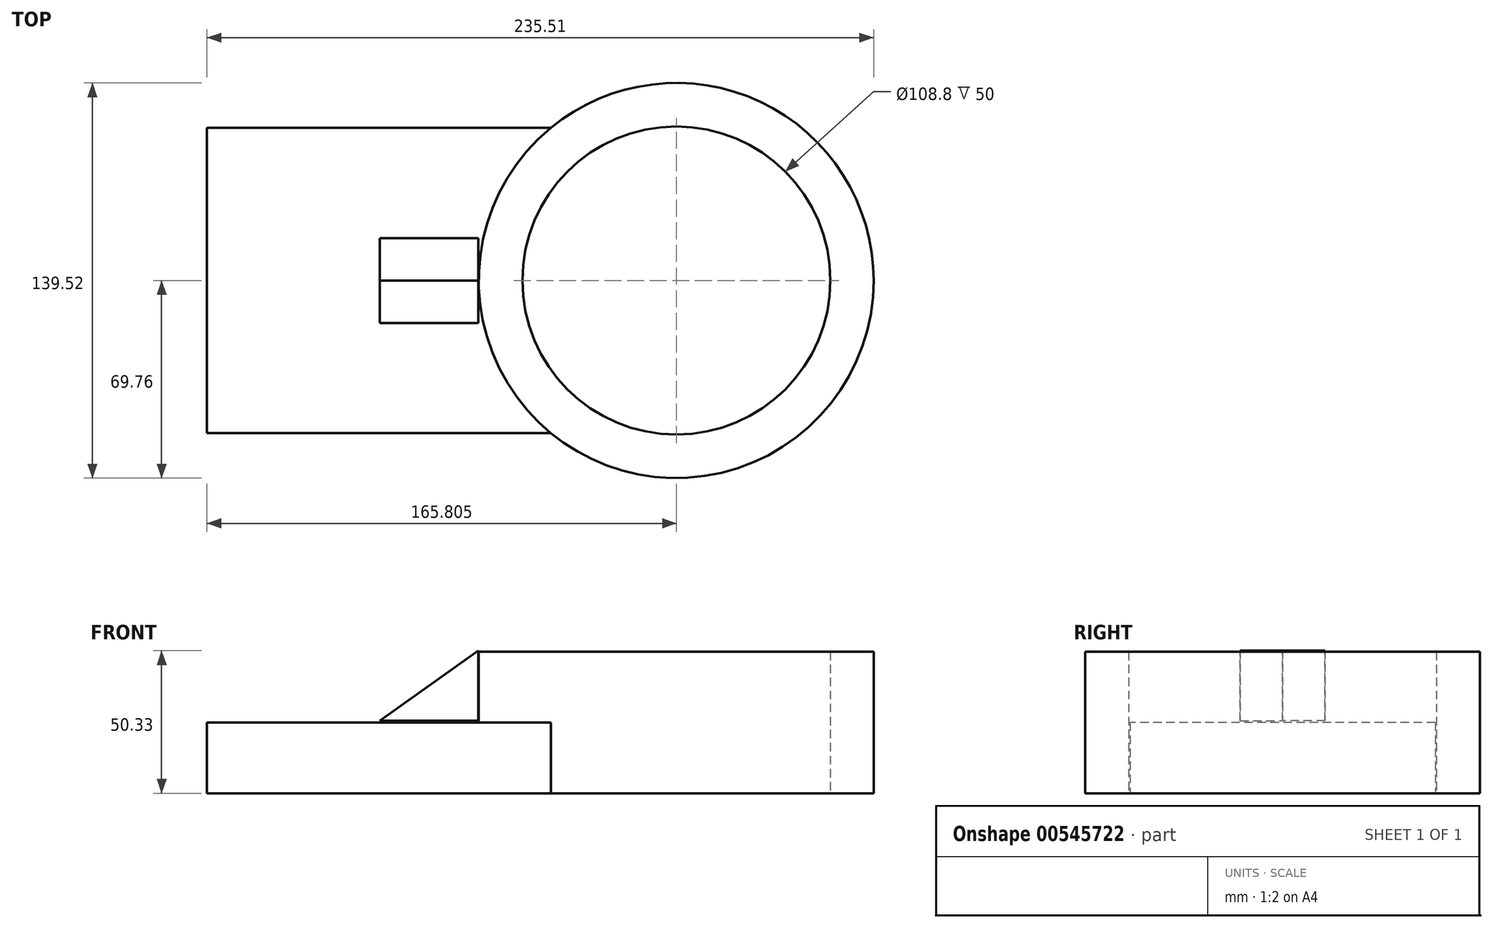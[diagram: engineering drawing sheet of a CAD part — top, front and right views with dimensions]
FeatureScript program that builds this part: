
annotation { "Feature Type Name" : "Feature", "Feature Type Description" : "" }
export const myFeature = defineFeature(function(context is Context, id is Id, definition is map)
    precondition{}
    {
        {
            var Q0;
            Q0=qCreatedBy(makeId("Top.planeOp"),FACE);
            var sketch = newSketch(context, id + "F0", { "sketchPlane" : qUnion([Q0])});
            skLineSegment(sketch, "E0.bottom", {"start": v(-61.03, 53.9) * mm, "end": v(61.03, 53.9) * mm});
            skLineSegment(sketch, "E0.top", {"start": v(-61.03, -53.9) * mm, "end": v(61.03, -53.9) * mm});
            skLineSegment(sketch, "E0.left", {"start": v(-61.03, 53.9) * mm, "end": v(-61.03, -53.9) * mm});
            skPoint(sketch, "E0.middle", {"position": v(0, 0) * mm});
            skArc(sketch, "E1", {"start": v(61.03, 53.9) * mm, "mid": v(35.53, 0) * mm, "end": v(61.03, -53.9) * mm});
            skSolve(sketch);
        }
        {
            var Q0;
            Q0=qCreatedBy(makeId("Top.planeOp"),FACE);
            var sketch = newSketch(context, id + "F1", { "sketchPlane" : qUnion([Q0])});
            skCircle(sketch, "E2", {"center": v(104.72, 0) * mm, "radius": 69.76 * mm});
            skSolve(sketch);
        }
        {
            var Q0;
            Q0 = qSketchRegion(id + "F0", true);
            extrude(context, id + "F2", {"entities" : qUnion([Q0]), "depth" : 25 * mm, "offsetDistance" : 25 * mm});
        }
        {
            var Q0;
            Q0=qCreatedBy(makeId("Top.planeOp"),FACE);
            var sketch = newSketch(context, id + "F3", { "sketchPlane" : qUnion([Q0])});
            skCircle(sketch, "E3", {"center": v(104.78, 0) * mm, "radius": 54.4 * mm});
            skSolve(sketch);
        }
        {
            var Q0;
            Q0 = qSketchRegion(id + "F1", true);
            extrude(context, id + "F4", {"entities" : qUnion([Q0]), "operationType" : NewBodyOperationType.ADD, "depth" : 50 * mm, "offsetDistance" : 25 * mm});
        }
        {
            var Q0;
            Q0=makeQuery(id+"F3.imprint","IMPRINT",FACE,{"disambiguationData":[TD([[makeQuery(id+"F3.imprint","IMPRINT",EDGE,{"derivedFrom":sQuery(id+"F3.wireOp",EDGE,"E3")}),1.0]])]});
            extrude(context, id + "F5", {"entities" : qUnion([Q0]), "operationType" : NewBodyOperationType.REMOVE, "depth" : 50 * mm, "offsetDistance" : 25 * mm});
        }
        {
            var Q0;
            Q0=qCreatedBy(makeId("Front.planeOp"),FACE);
            var sketch = newSketch(context, id + "F6", { "sketchPlane" : qUnion([Q0])});
            skLineSegment(sketch, "E4", {"start": v(34.81, 50.33) * mm, "end": v(0, 25.66) * mm});
            skLineSegment(sketch, "E5", {"start": v(0, 25.66) * mm, "end": v(34.81, 25.66) * mm});
            skLineSegment(sketch, "E6", {"start": v(34.81, 25.66) * mm, "end": v(34.81, 50.33) * mm});
            skSolve(sketch);
        }
        {
            var Q0;
            Q0 = qSketchRegion(id + "F6", true);
            extrude(context, id + "F7", {"entities" : qUnion([Q0]), "depth" : 15 * mm, "offsetDistance" : 25 * mm});
        }
        {
            var Q0;
            Q0=makeQuery(id+"F7.opExtrude","SWEPT_BODY",BODY,{"disambiguationData":[OSD([sQuery(id+"F6.wireOp",EDGE,"E4"),sQuery(id+"F6.wireOp",EDGE,"E5"),sQuery(id+"F6.wireOp",EDGE,"E6")])]});
            var Q1;
            Q1=makeQuery(id+"F7.opExtrude","CAP_FACE",FACE,{"disambiguationData":[OSD([sQuery(id+"F6.wireOp",EDGE,"E4"),sQuery(id+"F6.wireOp",EDGE,"E5"),sQuery(id+"F6.wireOp",EDGE,"E6")])],"isStart":true});
            mirror(context, id + "F8", {"operationType" : NewBodyOperationType.ADD, "entities" : qUnion([Q0]), "mirrorPlane" : qUnion([Q1])});
        }
    });
